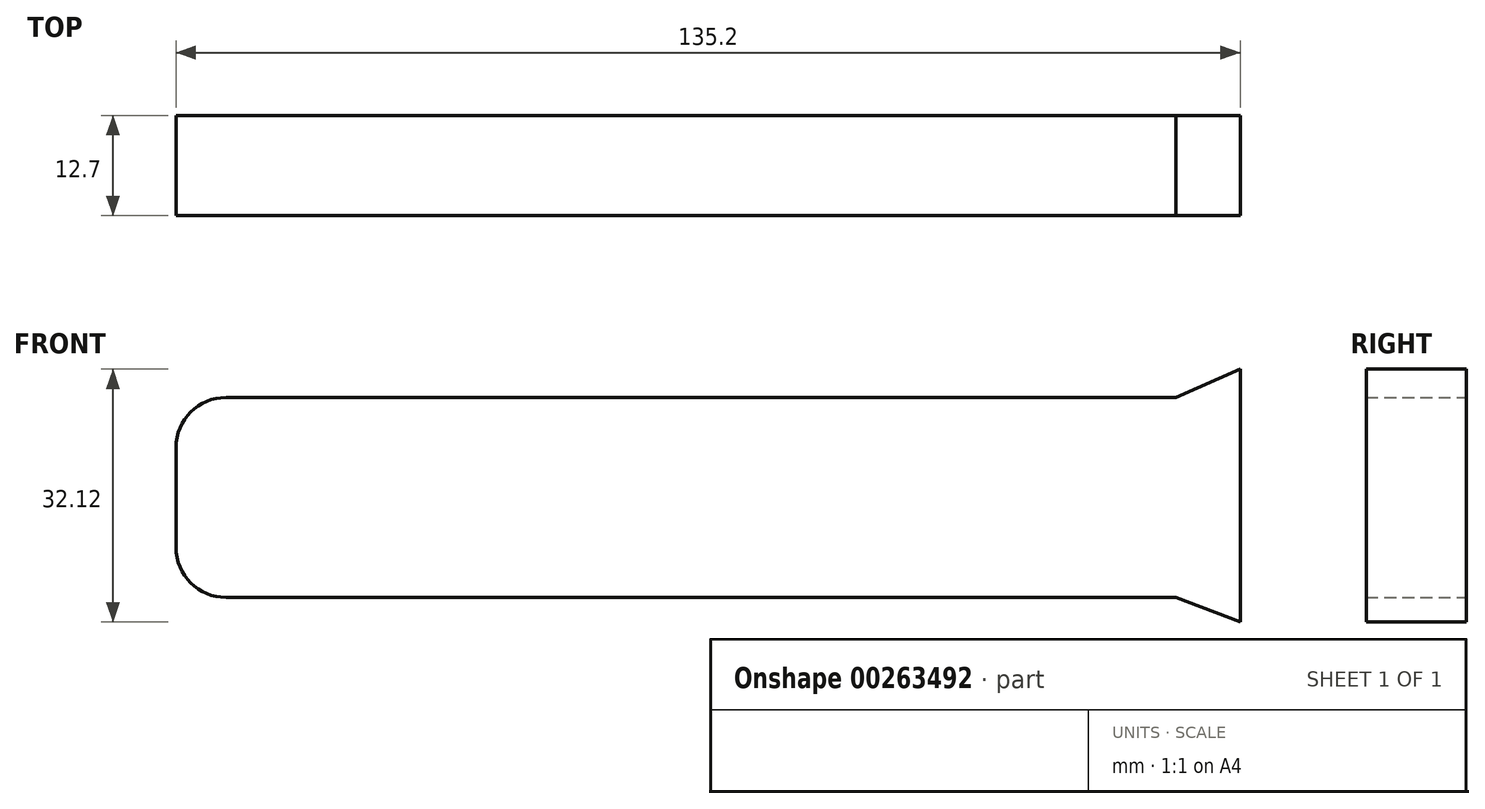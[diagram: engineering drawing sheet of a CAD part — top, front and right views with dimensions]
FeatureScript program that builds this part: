
annotation { "Feature Type Name" : "Feature", "Feature Type Description" : "" }
export const myFeature = defineFeature(function(context is Context, id is Id, definition is map)
    precondition{}
    {
        {
            var Q0;
            Q0=qCreatedBy(makeId("Front.planeOp"),FACE);
            var sketch = newSketch(context, id + "F0", { "sketchPlane" : qUnion([Q0])});
            skLineSegment(sketch, "E0.bottom", {"start": v(-57.15, 12.7) * mm, "end": v(63.5, 12.7) * mm});
            skLineSegment(sketch, "E0.top", {"start": v(-57.15, -12.7) * mm, "end": v(63.5, -12.7) * mm});
            skLineSegment(sketch, "E0.left", {"start": v(-63.5, 6.35) * mm, "end": v(-63.5, -6.35) * mm});
            skLineSegment(sketch, "E0.right", {"start": v(63.5, 12.7) * mm, "end": v(63.5, -12.7) * mm});
            skPoint(sketch, "E0.middle", {"position": v(0, 0) * mm});
            skLineSegment(sketch, "E1", {"start": v(63.5, 12.7) * mm, "end": v(71.7, 16.3) * mm});
            skLineSegment(sketch, "E2", {"start": v(71.7, 16.3) * mm, "end": v(71.7, -15.81) * mm});
            skLineSegment(sketch, "E3", {"start": v(71.7, -15.81) * mm, "end": v(63.5, -12.7) * mm});
            skPoint(sketch, "E4.visualSharp", {"position": v(-63.5, 12.7) * mm});
            skArc(sketch, "E4.filletArc", {"start": v(-57.15, 12.7) * mm, "mid": v(-61.64, 10.84) * mm, "end": v(-63.5, 6.35) * mm});
            skPoint(sketch, "E5.visualSharp", {"position": v(-63.5, -12.7) * mm});
            skArc(sketch, "E5.filletArc", {"start": v(-63.5, -6.35) * mm, "mid": v(-61.64, -10.84) * mm, "end": v(-57.15, -12.7) * mm});
            skSolve(sketch);
        }
        {
            var Q0;
            Q0=makeQuery(id+"F0.imprint","IMPRINT",FACE,{"disambiguationData":[TD([[makeQuery(id+"F0.imprint","IMPRINT",EDGE,{"derivedFrom":sQuery(id+"F0.wireOp",EDGE,"E0.right")}),1.0]])]});
            var Q1;
            Q1=makeQuery(id+"F0.imprint","IMPRINT",FACE,{"disambiguationData":[TD([[makeQuery(id+"F0.imprint","IMPRINT",EDGE,{"derivedFrom":sQuery(id+"F0.wireOp",EDGE,"E0.bottom")}),-1.0]])]});
            extrude(context, id + "F1", {"entities" : qUnion([Q0, Q1]), "depth" : 12.7 * mm});
        }
    });
